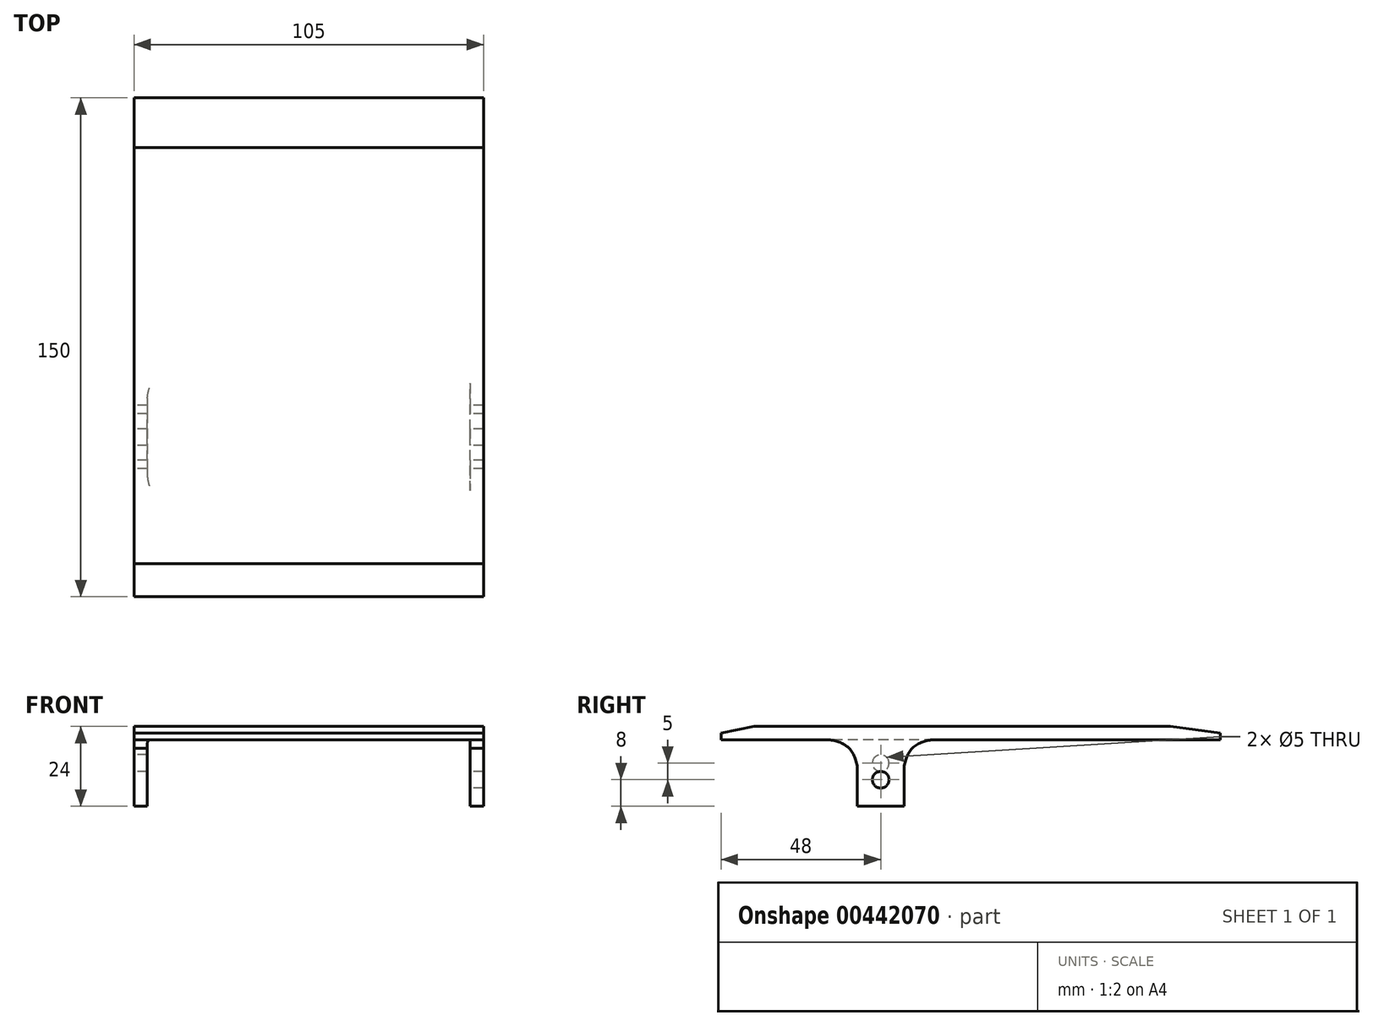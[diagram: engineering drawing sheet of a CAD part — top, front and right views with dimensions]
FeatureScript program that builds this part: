
annotation { "Feature Type Name" : "Feature", "Feature Type Description" : "" }
export const myFeature = defineFeature(function(context is Context, id is Id, definition is map)
    precondition{}
    {
        {
            var Q0;
            Q0=qCreatedBy(makeId("Right.planeOp"),FACE);
            var sketch = newSketch(context, id + "F0", { "sketchPlane" : qUnion([Q0])});
            skLineSegment(sketch, "E0.bottom", {"start": v(0, 0) * mm, "end": v(150, 0) * mm});
            skLineSegment(sketch, "E0.top", {"start": v(0, -4) * mm, "end": v(41, -4) * mm});
            skLineSegment(sketch, "E0.left", {"start": v(0, 0) * mm, "end": v(0, -4) * mm});
            skLineSegment(sketch, "E0.right", {"start": v(150, 0) * mm, "end": v(150, -4) * mm});
            skLineSegment(sketch, "E1", {"start": v(41, -24) * mm, "end": v(41, -4) * mm});
            skLineSegment(sketch, "E2", {"start": v(55, -24) * mm, "end": v(55, -4) * mm});
            skLineSegment(sketch, "E3.trimOffspring", {"start": v(55, -4) * mm, "end": v(150, -4) * mm});
            skLineSegment(sketch, "E4", {"start": v(41, -24) * mm, "end": v(55, -24) * mm});
            skSolve(sketch);
        }
        {
            var Q0;
            Q0 = qSketchRegion(id + "F0", true);
            extrude(context, id + "F1", {"entities" : qUnion([Q0]), "depth" : 4 * mm});
        }
        {
            var Q0;
            Q0=qCreatedBy(makeId("Right.planeOp"),FACE);
            var sketch = newSketch(context, id + "F2", { "sketchPlane" : qUnion([Q0])});
            skLineSegment(sketch, "E5.bottom", {"start": v(0, 0) * mm, "end": v(150, 0) * mm});
            skLineSegment(sketch, "E5.top", {"start": v(0, -4) * mm, "end": v(150, -4) * mm});
            skLineSegment(sketch, "E5.left", {"start": v(0, 0) * mm, "end": v(0, -4) * mm});
            skLineSegment(sketch, "E5.right", {"start": v(150, 0) * mm, "end": v(150, -4) * mm});
            skSolve(sketch);
        }
        {
            var Q0;
            Q0 = qSketchRegion(id + "F2", true);
            extrude(context, id + "F3", {"entities" : qUnion([Q0]), "operationType" : NewBodyOperationType.ADD, "depth" : 101 * mm, "hasSecondDirection" : true, "secondDirectionOppositeDirection" : false, "secondDirectionDepth" : 3 * mm});
        }
        {
            var Q0;
            Q0 = qSketchRegion(id + "F0", true);
            extrude(context, id + "F4", {"entities" : qUnion([Q0]), "operationType" : NewBodyOperationType.ADD, "depth" : 105 * mm, "hasSecondDirection" : true, "secondDirectionOppositeDirection" : false, "secondDirectionDepth" : 101 * mm});
        }
        {
            var Q0;
            Q0=qCreatedBy(makeId("Right.planeOp"),FACE);
            var sketch = newSketch(context, id + "F5", { "sketchPlane" : qUnion([Q0])});
            skCircle(sketch, "E6", {"center": v(48, -16) * mm, "radius": 2.5 * mm});
            skCircle(sketch, "E7", {"center": v(48, -11) * mm, "radius": 2.5 * mm});
            skSolve(sketch);
        }
        {
            var Q0;
            Q0=makeQuery(id+"F5.imprint","IMPRINT",FACE,{"disambiguationData":[TD([[makeQuery(id+"F5.imprint","IMPRINT",EDGE,{"derivedFrom":sQuery(id+"F5.wireOp",EDGE,"E6")}),1.0]])]});
            extrude(context, id + "F6", {"entities" : qUnion([Q0]), "operationType" : NewBodyOperationType.REMOVE, "depth" : 105 * mm, "hasSecondDirection" : true, "secondDirectionOppositeDirection" : false, "secondDirectionDepth" : 25 * mm});
        }
        {
            var Q0;
            Q0=makeQuery(id+"F1.opExtrude","SWEPT_EDGE",EDGE,{"disambiguationData":[OSD([sQuery(id+"F0.wireOp",EDGE,"E0.top"),sQuery(id+"F0.wireOp",EDGE,"E1")])]});
            var Q1;
            Q1=makeQuery(id+"F4.opExtrude","SWEPT_EDGE",EDGE,{"disambiguationData":[OSD([sQuery(id+"F0.wireOp",EDGE,"E0.top"),sQuery(id+"F0.wireOp",EDGE,"E1")])]});
            var Q2;
            Q2=makeQuery(id+"F4.opExtrude","SWEPT_EDGE",EDGE,{"disambiguationData":[OSD([sQuery(id+"F0.wireOp",EDGE,"E2"),sQuery(id+"F0.wireOp",EDGE,"E3.trimOffspring")])]});
            var Q3;
            Q3=makeQuery(id+"F1.opExtrude","SWEPT_EDGE",EDGE,{"disambiguationData":[OSD([sQuery(id+"F0.wireOp",EDGE,"E2"),sQuery(id+"F0.wireOp",EDGE,"E3.trimOffspring")])]});
            chamfer(context, id + "F7", {"entities" : qUnion([Q0, Q1, Q2, Q3]), "width" : 5 * mm, "tangentPropagation" : true});
        }
        {
            var Q0;
            Q0=makeQuery(id+"F5.imprint","IMPRINT",FACE,{"disambiguationData":[TD([[makeQuery(id+"F5.imprint","IMPRINT",EDGE,{"derivedFrom":sQuery(id+"F5.wireOp",EDGE,"E7")}),1.0]])]});
            extrude(context, id + "F8", {"entities" : qUnion([Q0]), "operationType" : NewBodyOperationType.REMOVE, "depth" : 25 * mm});
        }
        {
            var Q0;
            Q0=makeQuery(id+"F3.opExtrude","CAP_EDGE",EDGE,{"disambiguationData":[OSD([sQuery(id+"F2.wireOp",EDGE,"E5.top")])],"isStart":false});
            var Q1;
            Q1=makeQuery(id+"F3.boolean.opBoolean","INTERSECT",EDGE,{"derivedFrom":[makeQuery(id+"F1.opExtrude","CAP_FACE",FACE,{"disambiguationData":[OSD([sQuery(id+"F0.wireOp",EDGE,"E0.bottom"),sQuery(id+"F0.wireOp",EDGE,"E0.top"),sQuery(id+"F0.wireOp",EDGE,"E0.left"),sQuery(id+"F0.wireOp",EDGE,"E0.right"),sQuery(id+"F0.wireOp",EDGE,"E1"),sQuery(id+"F0.wireOp",EDGE,"E2"),sQuery(id+"F0.wireOp",EDGE,"E3.trimOffspring"),sQuery(id+"F0.wireOp",EDGE,"E4")])],"isStart":false}),makeQuery(id+"F3.opExtrude","SWEPT_FACE",FACE,{"disambiguationData":[OSD([sQuery(id+"F2.wireOp",EDGE,"E5.top")])]})]});
            fillet(context, id + "F9", {"entities" : qUnion([Q0, Q1]), "radius" : 1 * mm, "tangentPropagation" : true, "allowEdgeOverflow" : false});
        }
        {
            var Q0;
            {var subQ0=sQuery(id+"F0.wireOp",EDGE,"E0.left");var subQ1=sQuery(id+"F0.wireOp",EDGE,"E0.bottom");Q0=makeQuery(id+"F4.boolean.opBoolean","MERGE",EDGE,{"derivedFrom":[makeQuery(id+"F3.boolean.opBoolean","MERGE",EDGE,{"derivedFrom":[makeQuery(id+"F1.opExtrude","SWEPT_EDGE",EDGE,{"disambiguationData":[OSD([subQ1,subQ0])]}),makeQuery(id+"F3.opExtrude","SWEPT_EDGE",EDGE,{"disambiguationData":[OSD([sQuery(id+"F2.wireOp",EDGE,"E5.bottom"),sQuery(id+"F2.wireOp",EDGE,"E5.left")])]})]}),makeQuery(id+"F4.opExtrude","SWEPT_EDGE",EDGE,{"disambiguationData":[OSD([subQ1,subQ0])]})]});}
            chamfer(context, id + "F10", {"entities" : qUnion([Q0]), "chamferType" : ChamferType.TWO_OFFSETS, "width1" : 2 * mm, "oppositeDirection" : false, "width2" : 10 * mm, "tangentPropagation" : true});
        }
        {
            var Q0;
            {var subQ0=sQuery(id+"F0.wireOp",EDGE,"E0.right");var subQ1=sQuery(id+"F0.wireOp",EDGE,"E0.bottom");Q0=makeQuery(id+"F4.boolean.opBoolean","MERGE",EDGE,{"derivedFrom":[makeQuery(id+"F3.boolean.opBoolean","MERGE",EDGE,{"derivedFrom":[makeQuery(id+"F1.opExtrude","SWEPT_EDGE",EDGE,{"disambiguationData":[OSD([subQ1,subQ0])]}),makeQuery(id+"F3.opExtrude","SWEPT_EDGE",EDGE,{"disambiguationData":[OSD([sQuery(id+"F2.wireOp",EDGE,"E5.bottom"),sQuery(id+"F2.wireOp",EDGE,"E5.right")])]})]}),makeQuery(id+"F4.opExtrude","SWEPT_EDGE",EDGE,{"disambiguationData":[OSD([subQ1,subQ0])]})]});}
            chamfer(context, id + "F11", {"entities" : qUnion([Q0]), "chamferType" : ChamferType.TWO_OFFSETS, "width1" : 15 * mm, "oppositeDirection" : false, "width2" : 2 * mm, "tangentPropagation" : true});
        }
        {
            var Q0;
            {var subQ0=sQuery(id+"F0.wireOp",EDGE,"E3.trimOffspring");var subQ1=sQuery(id+"F0.wireOp",EDGE,"E0.top");Q0=makeQuery(id+"F7.opChamfer","BLEND_EDGE",EDGE,{"blendedFrom":[makeQuery(id+"F4.opExtrude","SWEPT_EDGE",EDGE,{"disambiguationData":[OSD([subQ1,sQuery(id+"F0.wireOp",EDGE,"E1")])]}),makeQuery(id+"F4.boolean.opBoolean","MERGE",FACE,{"derivedFrom":[makeQuery(id+"F3.boolean.opBoolean","MERGE",FACE,{"derivedFrom":[makeQuery(id+"F1.opExtrude","SWEPT_FACE",FACE,{"disambiguationData":[OSD([subQ1])]}),makeQuery(id+"F1.opExtrude","SWEPT_FACE",FACE,{"disambiguationData":[OSD([subQ0])]}),makeQuery(id+"F3.opExtrude","SWEPT_FACE",FACE,{"disambiguationData":[OSD([sQuery(id+"F2.wireOp",EDGE,"E5.top")])]})]}),makeQuery(id+"F4.opExtrude","SWEPT_FACE",FACE,{"disambiguationData":[OSD([subQ1])]}),makeQuery(id+"F4.opExtrude","SWEPT_FACE",FACE,{"disambiguationData":[OSD([subQ0])]})]})],"blendedInto":[makeQuery(id+"F4.boolean.opBoolean","MERGE",FACE,{"derivedFrom":[makeQuery(id+"F3.boolean.opBoolean","MERGE",FACE,{"derivedFrom":[makeQuery(id+"F1.opExtrude","SWEPT_FACE",FACE,{"disambiguationData":[OSD([subQ1])]}),makeQuery(id+"F1.opExtrude","SWEPT_FACE",FACE,{"disambiguationData":[OSD([subQ0])]}),makeQuery(id+"F3.opExtrude","SWEPT_FACE",FACE,{"disambiguationData":[OSD([sQuery(id+"F2.wireOp",EDGE,"E5.top")])]})]}),makeQuery(id+"F4.opExtrude","SWEPT_FACE",FACE,{"disambiguationData":[OSD([subQ1])]}),makeQuery(id+"F4.opExtrude","SWEPT_FACE",FACE,{"disambiguationData":[OSD([subQ0])]})]})]});}
            var Q1;
            {var subQ0=sQuery(id+"F0.wireOp",EDGE,"E1");Q1=makeQuery(id+"F7.opChamfer","BLEND_EDGE",EDGE,{"blendedFrom":[makeQuery(id+"F4.opExtrude","SWEPT_EDGE",EDGE,{"disambiguationData":[OSD([sQuery(id+"F0.wireOp",EDGE,"E0.top"),subQ0])]}),makeQuery(id+"F4.opExtrude","SWEPT_FACE",FACE,{"disambiguationData":[OSD([subQ0])]})],"blendedInto":[makeQuery(id+"F4.opExtrude","SWEPT_FACE",FACE,{"disambiguationData":[OSD([subQ0])]})]});}
            var Q2;
            {var subQ0=sQuery(id+"F0.wireOp",EDGE,"E3.trimOffspring");var subQ1=sQuery(id+"F0.wireOp",EDGE,"E0.top");Q2=makeQuery(id+"F7.opChamfer","BLEND_EDGE",EDGE,{"blendedFrom":[makeQuery(id+"F1.opExtrude","SWEPT_EDGE",EDGE,{"disambiguationData":[OSD([subQ1,sQuery(id+"F0.wireOp",EDGE,"E1")])]}),makeQuery(id+"F4.boolean.opBoolean","MERGE",FACE,{"derivedFrom":[makeQuery(id+"F3.boolean.opBoolean","MERGE",FACE,{"derivedFrom":[makeQuery(id+"F1.opExtrude","SWEPT_FACE",FACE,{"disambiguationData":[OSD([subQ1])]}),makeQuery(id+"F1.opExtrude","SWEPT_FACE",FACE,{"disambiguationData":[OSD([subQ0])]}),makeQuery(id+"F3.opExtrude","SWEPT_FACE",FACE,{"disambiguationData":[OSD([sQuery(id+"F2.wireOp",EDGE,"E5.top")])]})]}),makeQuery(id+"F4.opExtrude","SWEPT_FACE",FACE,{"disambiguationData":[OSD([subQ1])]}),makeQuery(id+"F4.opExtrude","SWEPT_FACE",FACE,{"disambiguationData":[OSD([subQ0])]})]})],"blendedInto":[makeQuery(id+"F4.boolean.opBoolean","MERGE",FACE,{"derivedFrom":[makeQuery(id+"F3.boolean.opBoolean","MERGE",FACE,{"derivedFrom":[makeQuery(id+"F1.opExtrude","SWEPT_FACE",FACE,{"disambiguationData":[OSD([subQ1])]}),makeQuery(id+"F1.opExtrude","SWEPT_FACE",FACE,{"disambiguationData":[OSD([subQ0])]}),makeQuery(id+"F3.opExtrude","SWEPT_FACE",FACE,{"disambiguationData":[OSD([sQuery(id+"F2.wireOp",EDGE,"E5.top")])]})]}),makeQuery(id+"F4.opExtrude","SWEPT_FACE",FACE,{"disambiguationData":[OSD([subQ1])]}),makeQuery(id+"F4.opExtrude","SWEPT_FACE",FACE,{"disambiguationData":[OSD([subQ0])]})]})]});}
            var Q3;
            {var subQ0=sQuery(id+"F0.wireOp",EDGE,"E1");Q3=makeQuery(id+"F7.opChamfer","BLEND_EDGE",EDGE,{"blendedFrom":[makeQuery(id+"F1.opExtrude","SWEPT_EDGE",EDGE,{"disambiguationData":[OSD([sQuery(id+"F0.wireOp",EDGE,"E0.top"),subQ0])]}),makeQuery(id+"F1.opExtrude","SWEPT_FACE",FACE,{"disambiguationData":[OSD([subQ0])]})],"blendedInto":[makeQuery(id+"F1.opExtrude","SWEPT_FACE",FACE,{"disambiguationData":[OSD([subQ0])]})]});}
            var Q4;
            {var subQ0=sQuery(id+"F0.wireOp",EDGE,"E3.trimOffspring");var subQ1=sQuery(id+"F0.wireOp",EDGE,"E0.top");Q4=makeQuery(id+"F7.opChamfer","BLEND_EDGE",EDGE,{"blendedFrom":[makeQuery(id+"F4.opExtrude","SWEPT_EDGE",EDGE,{"disambiguationData":[OSD([sQuery(id+"F0.wireOp",EDGE,"E2"),subQ0])]}),makeQuery(id+"F4.boolean.opBoolean","MERGE",FACE,{"derivedFrom":[makeQuery(id+"F3.boolean.opBoolean","MERGE",FACE,{"derivedFrom":[makeQuery(id+"F1.opExtrude","SWEPT_FACE",FACE,{"disambiguationData":[OSD([subQ1])]}),makeQuery(id+"F1.opExtrude","SWEPT_FACE",FACE,{"disambiguationData":[OSD([subQ0])]}),makeQuery(id+"F3.opExtrude","SWEPT_FACE",FACE,{"disambiguationData":[OSD([sQuery(id+"F2.wireOp",EDGE,"E5.top")])]})]}),makeQuery(id+"F4.opExtrude","SWEPT_FACE",FACE,{"disambiguationData":[OSD([subQ1])]}),makeQuery(id+"F4.opExtrude","SWEPT_FACE",FACE,{"disambiguationData":[OSD([subQ0])]})]})],"blendedInto":[makeQuery(id+"F4.boolean.opBoolean","MERGE",FACE,{"derivedFrom":[makeQuery(id+"F3.boolean.opBoolean","MERGE",FACE,{"derivedFrom":[makeQuery(id+"F1.opExtrude","SWEPT_FACE",FACE,{"disambiguationData":[OSD([subQ1])]}),makeQuery(id+"F1.opExtrude","SWEPT_FACE",FACE,{"disambiguationData":[OSD([subQ0])]}),makeQuery(id+"F3.opExtrude","SWEPT_FACE",FACE,{"disambiguationData":[OSD([sQuery(id+"F2.wireOp",EDGE,"E5.top")])]})]}),makeQuery(id+"F4.opExtrude","SWEPT_FACE",FACE,{"disambiguationData":[OSD([subQ1])]}),makeQuery(id+"F4.opExtrude","SWEPT_FACE",FACE,{"disambiguationData":[OSD([subQ0])]})]})]});}
            var Q5;
            {var subQ0=sQuery(id+"F0.wireOp",EDGE,"E3.trimOffspring");var subQ1=sQuery(id+"F0.wireOp",EDGE,"E0.top");Q5=makeQuery(id+"F7.opChamfer","BLEND_EDGE",EDGE,{"blendedFrom":[makeQuery(id+"F1.opExtrude","SWEPT_EDGE",EDGE,{"disambiguationData":[OSD([sQuery(id+"F0.wireOp",EDGE,"E2"),subQ0])]}),makeQuery(id+"F4.boolean.opBoolean","MERGE",FACE,{"derivedFrom":[makeQuery(id+"F3.boolean.opBoolean","MERGE",FACE,{"derivedFrom":[makeQuery(id+"F1.opExtrude","SWEPT_FACE",FACE,{"disambiguationData":[OSD([subQ1])]}),makeQuery(id+"F1.opExtrude","SWEPT_FACE",FACE,{"disambiguationData":[OSD([subQ0])]}),makeQuery(id+"F3.opExtrude","SWEPT_FACE",FACE,{"disambiguationData":[OSD([sQuery(id+"F2.wireOp",EDGE,"E5.top")])]})]}),makeQuery(id+"F4.opExtrude","SWEPT_FACE",FACE,{"disambiguationData":[OSD([subQ1])]}),makeQuery(id+"F4.opExtrude","SWEPT_FACE",FACE,{"disambiguationData":[OSD([subQ0])]})]})],"blendedInto":[makeQuery(id+"F4.boolean.opBoolean","MERGE",FACE,{"derivedFrom":[makeQuery(id+"F3.boolean.opBoolean","MERGE",FACE,{"derivedFrom":[makeQuery(id+"F1.opExtrude","SWEPT_FACE",FACE,{"disambiguationData":[OSD([subQ1])]}),makeQuery(id+"F1.opExtrude","SWEPT_FACE",FACE,{"disambiguationData":[OSD([subQ0])]}),makeQuery(id+"F3.opExtrude","SWEPT_FACE",FACE,{"disambiguationData":[OSD([sQuery(id+"F2.wireOp",EDGE,"E5.top")])]})]}),makeQuery(id+"F4.opExtrude","SWEPT_FACE",FACE,{"disambiguationData":[OSD([subQ1])]}),makeQuery(id+"F4.opExtrude","SWEPT_FACE",FACE,{"disambiguationData":[OSD([subQ0])]})]})]});}
            var Q6;
            {var subQ0=sQuery(id+"F0.wireOp",EDGE,"E2");Q6=makeQuery(id+"F7.opChamfer","BLEND_EDGE",EDGE,{"blendedFrom":[makeQuery(id+"F1.opExtrude","SWEPT_EDGE",EDGE,{"disambiguationData":[OSD([subQ0,sQuery(id+"F0.wireOp",EDGE,"E3.trimOffspring")])]}),makeQuery(id+"F1.opExtrude","SWEPT_FACE",FACE,{"disambiguationData":[OSD([subQ0])]})],"blendedInto":[makeQuery(id+"F1.opExtrude","SWEPT_FACE",FACE,{"disambiguationData":[OSD([subQ0])]})]});}
            var Q7;
            {var subQ0=sQuery(id+"F0.wireOp",EDGE,"E2");Q7=makeQuery(id+"F7.opChamfer","BLEND_EDGE",EDGE,{"blendedFrom":[makeQuery(id+"F4.opExtrude","SWEPT_EDGE",EDGE,{"disambiguationData":[OSD([subQ0,sQuery(id+"F0.wireOp",EDGE,"E3.trimOffspring")])]}),makeQuery(id+"F4.opExtrude","SWEPT_FACE",FACE,{"disambiguationData":[OSD([subQ0])]})],"blendedInto":[makeQuery(id+"F4.opExtrude","SWEPT_FACE",FACE,{"disambiguationData":[OSD([subQ0])]})]});}
            fillet(context, id + "F12", {"entities" : qUnion([Q0, Q1, Q2, Q3, Q4, Q5, Q6, Q7]), "radius" : 10 * mm, "tangentPropagation" : true, "allowEdgeOverflow" : false});
        }
    });
